# Revit family: Medical-Casework_Shield Casework_Nurse-Server-F2B
name_source: partatom
category: Casework
units: mm (PartAtom-declared; Revit-internal decimal feet)

## family parameters
Always vertical = Yes
Cut with Voids When Loaded = Yes
OmniClass Number = 23.40.35.17.34
OmniClass Title = Medical Casework
Room Calculation Point = No
Shared = No
Work Plane-Based = No

## types (4) — shared parameters
Assembly Code = E2010200
Depth = 24 "
Description = The Nurse Server F2B
Edition number = 1
Finish = Acrylic Solid Surface
Keynote = 12300
Manufacturer = Shield Casework
Model = The Nurse Server F2B
Product Guid = fc8e723f-7139-4298-8aeb-ef5974d179d6
Product Material = Shield Casework - Acrylic Solid Surface - S01 White
Product data url = https://www.bimobject.com
Product url = https://shieldheadwalls.com
URL = https://www.shieldcasework.com
|DwOpt01 = Drawer : 00 - None
|DwOpt02 = Drawer : 01 - Single Drawer
|DwOpt03 = Drawer : 02 - Double Drawer
|LckOpt01 = Lock : 00 - None
|LckOpt02 = Lock : 01 - MicroIQ Lock on Patient Room Side
|LckOpt03 = Lock : 02 - MicroIQ Lock on Corridor Side
|LckOpt04 = Lock : 03 - MicroIQ Lock on Both Sides
|PulOpt01 = Pull : 01 - Cut Through
|PulOpt02 = Pull : 02 - Solid Surface Recessed
|PulOpt03 = Pull : 03 - Wire Pull
|PulOpt04 = Pull : 04 - Continuous Tab
|TopOpt01 = Top : 01 - Flat Top
|TopOpt02 = Top : 02 - Sloped Top
|TopOpt03 = Top : 03 - Soffit
zero-valued in all types: Default Elevation

## per-type parameters (varying)
| type | Height | Width | /TopDorHgh | /TopDorWdth |
| 24" W x 72" H x 24" D | 72 " | 24 " | 35.03 " | 11.95 " |
| 24" W x 84" H x 24" D | 84 " | 24 " | 47.03 " | 11.95 " |
| 30" W x 72" H x 24" D | 72 " | 30 " | 35.03 " | 14.95 " |
| 30" W x 84" H x 24" D | 84 " | 30 " | 47.03 " | 14.95 " |

## geometry (parser evidence)
native form markers: Sweep x33
no freeform markers — native parametric forms only
